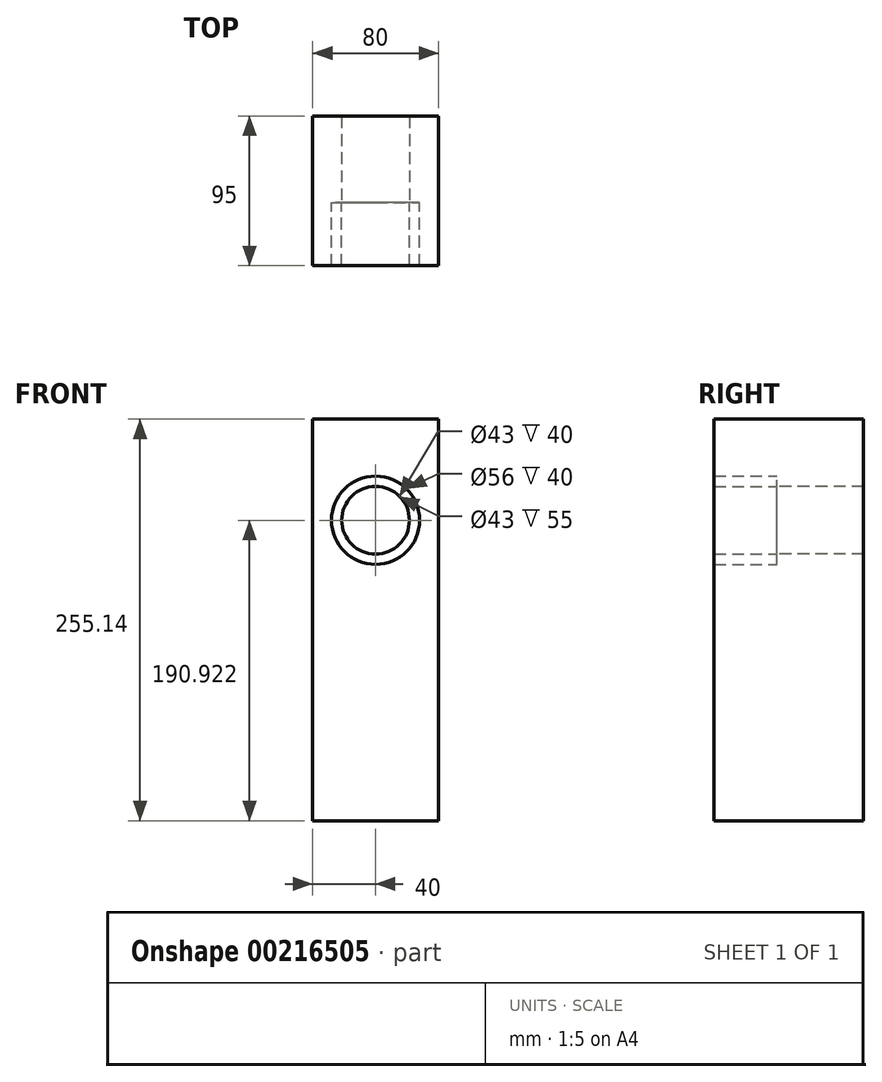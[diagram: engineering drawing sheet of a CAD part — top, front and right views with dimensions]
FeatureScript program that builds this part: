
annotation { "Feature Type Name" : "Feature", "Feature Type Description" : "" }
export const myFeature = defineFeature(function(context is Context, id is Id, definition is map)
    precondition{}
    {
        {
            var Q0;
            Q0=qCreatedBy(makeId("Front.planeOp"),FACE);
            var sketch = newSketch(context, id + "F0", { "sketchPlane" : qUnion([Q0])});
            skLineSegment(sketch, "E0.bottom", {"start": v(40, -127.57) * mm, "end": v(-40, -127.57) * mm});
            skLineSegment(sketch, "E0.top", {"start": v(40, 127.57) * mm, "end": v(-40, 127.57) * mm});
            skLineSegment(sketch, "E0.left", {"start": v(40, -127.57) * mm, "end": v(40, 127.57) * mm});
            skLineSegment(sketch, "E0.right", {"start": v(-40, -127.57) * mm, "end": v(-40, 127.57) * mm});
            skPoint(sketch, "E0.middle", {"position": v(0, 0) * mm});
            skSolve(sketch);
        }
        {
            var Q0;
            Q0 = qSketchRegion(id + "F0", true);
            extrude(context, id + "F1", {"entities" : qUnion([Q0]), "depth" : 95 * mm});
        }
        {
            var Q0;
            Q0=makeQuery(id+"F1.opExtrude","CAP_FACE",FACE,{"disambiguationData":[OSD([sQuery(id+"F0.wireOp",EDGE,"E0.bottom"),sQuery(id+"F0.wireOp",EDGE,"E0.top"),sQuery(id+"F0.wireOp",EDGE,"E0.left"),sQuery(id+"F0.wireOp",EDGE,"E0.right")])],"isStart":false});
            var sketch = newSketch(context, id + "F2", { "sketchPlane" : qUnion([Q0])});
            skCircle(sketch, "E1", {"center": v(0, 63.35) * mm, "radius": 28 * mm});
            skSolve(sketch);
        }
        {
            var Q0;
            Q0 = qSketchRegion(id + "F2", true);
            extrude(context, id + "F3", {"entities" : qUnion([Q0]), "operationType" : NewBodyOperationType.REMOVE, "oppositeDirection" : true, "depth" : 40 * mm});
        }
        {
            var Q0;
            Q0=makeQuery(id+"F3.boolean.opBoolean","COPY",FACE,{"derivedFrom":makeQuery(id+"F3.opExtrude","CAP_FACE",FACE,{"disambiguationData":[OSD([sQuery(id+"F2.wireOp",EDGE,"E1")])],"isStart":false})});
            var sketch = newSketch(context, id + "F4", { "sketchPlane" : qUnion([Q0])});
            skCircle(sketch, "E2", {"center": v(0, 63.35) * mm, "radius": 21.5 * mm});
            skSolve(sketch);
        }
        {
            var Q0;
            Q0 = qSketchRegion(id + "F4", true);
            extrude(context, id + "F5", {"entities" : qUnion([Q0]), "operationType" : NewBodyOperationType.REMOVE, "endBound" : BoundingType.THROUGH_ALL, "oppositeDirection" : true, "depth" : 25 * mm});
        }
        {
            var Q0;
            Q0=makeQuery(id+"F3.boolean.opBoolean","COPY",FACE,{"derivedFrom":makeQuery(id+"F3.opExtrude","CAP_FACE",FACE,{"disambiguationData":[OSD([sQuery(id+"F2.wireOp",EDGE,"E1")])],"isStart":false})});
            var sketch = newSketch(context, id + "F6", { "sketchPlane" : qUnion([Q0])});
            skCircle(sketch, "E3", {"center": v(0, 63.35) * mm, "radius": 28 * mm});
            skCircle(sketch, "E4", {"center": v(0, 63.35) * mm, "radius": 21.5 * mm});
            skSolve(sketch);
        }
        {
            var Q0;
            Q0 = qSketchRegion(id + "F6", true);
            extrude(context, id + "F7", {"entities" : qUnion([Q0]), "depth" : 40 * mm});
        }
    });
